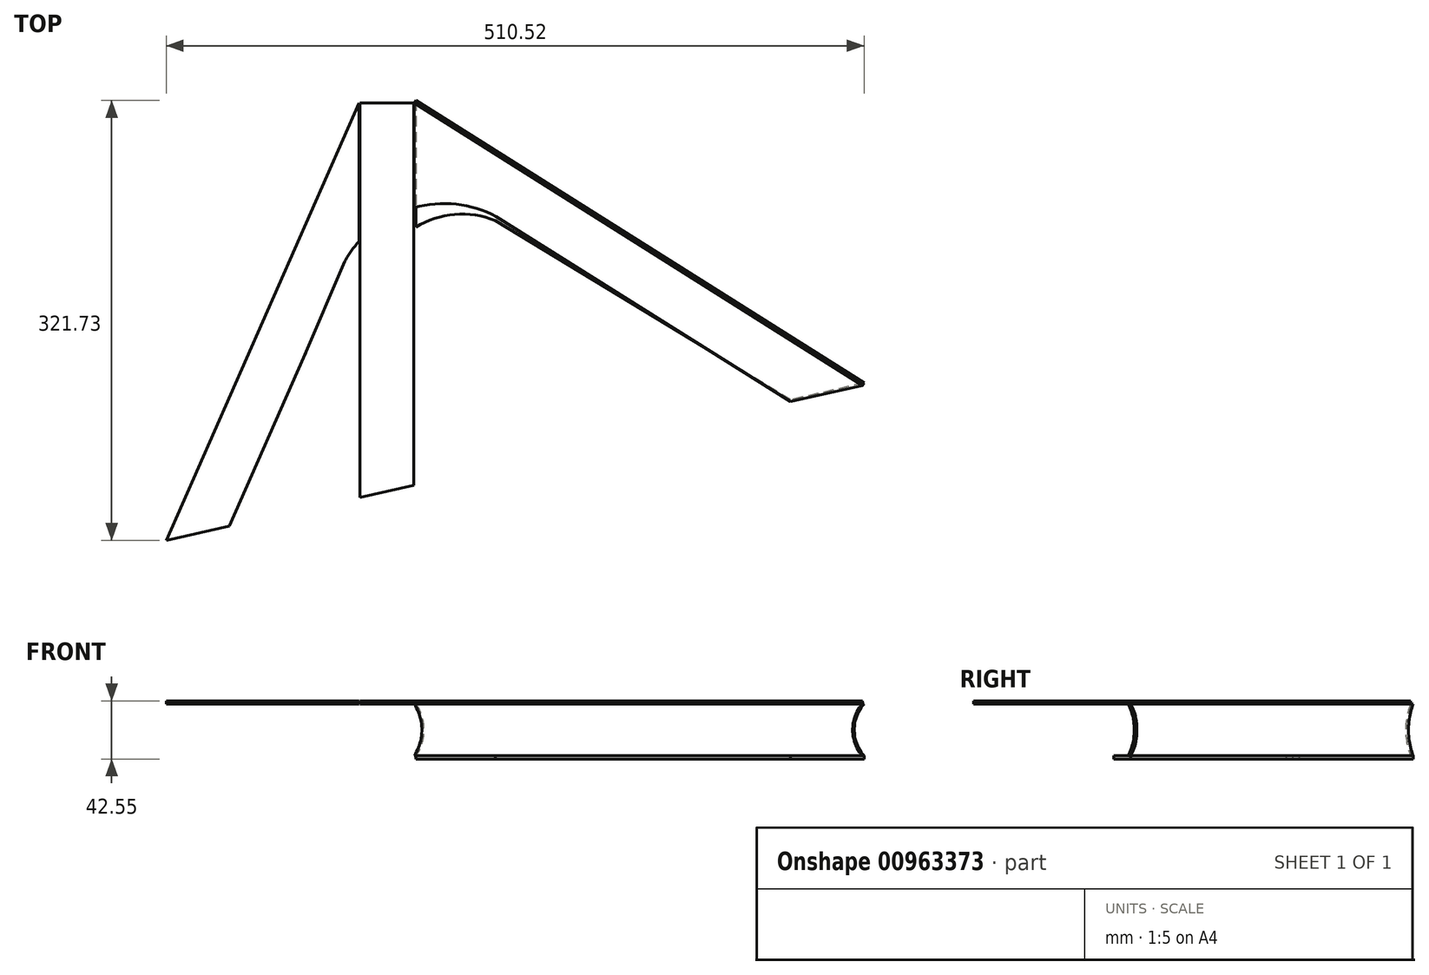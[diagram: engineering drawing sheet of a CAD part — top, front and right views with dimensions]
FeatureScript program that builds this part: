
annotation { "Feature Type Name" : "Feature", "Feature Type Description" : "" }
export const myFeature = defineFeature(function(context is Context, id is Id, definition is map)
    precondition{}
    {
        {
            var Q0;
            Q0=qCreatedBy(makeId("Top.planeOp"),FACE);
            var sketch = newSketch(context, id + "F0", { "sketchPlane" : qUnion([Q0])});
            skLineSegment(sketch, "E0", {"start": v(-23.6, 84.54) * mm, "end": v(27.72, 84.54) * mm, "construction": true});
            skLineSegment(sketch, "E1", {"start": v(27.72, 84.54) * mm, "end": v(27.72, -74.21) * mm, "construction": true});
            skLineSegment(sketch, "E2", {"start": v(27.72, -74.21) * mm, "end": v(-23.6, -74.21) * mm, "construction": true});
            skLineSegment(sketch, "E3", {"start": v(-23.6, -74.21) * mm, "end": v(-23.6, 84.54) * mm, "construction": true});
            skLineSegment(sketch, "E4", {"start": v(-152.74, -254.62) * mm, "end": v(367.67, -142.42) * mm, "construction": true});
            skLineSegment(sketch, "E5", {"start": v(367.67, -142.42) * mm, "end": v(27.72, 71.84) * mm, "construction": true});
            skLineSegment(sketch, "E6", {"start": v(-17.03, 71.84) * mm, "end": v(-158.62, -244.47) * mm, "construction": true});
            skLineSegment(sketch, "E7", {"start": v(-17.03, 71.84) * mm, "end": v(27.72, 71.84) * mm, "construction": true});
            skLineSegment(sketch, "E8", {"start": v(338.82, -22.65) * mm, "end": v(338.82, -196.3) * mm, "construction": true});
            skLineSegment(sketch, "E9", {"start": v(-227.54, -196.3) * mm, "end": v(-99.7, -276.87) * mm, "construction": true});
            skLineSegment(sketch, "E10", {"start": v(-144.73, -236.9) * mm, "end": v(347.37, -127.64) * mm, "construction": true});
            skLineSegment(sketch, "E11", {"start": v(3.64, 141.29) * mm, "end": v(3.64, -110.73) * mm, "construction": true});
            skLineSegment(sketch, "E12", {"start": v(-17.7, 61.46) * mm, "end": v(-17.7, -22.64) * mm});
            skLineSegment(sketch, "E13", {"start": v(-17.7, 61.46) * mm, "end": v(-17.7, 71.84) * mm});
            skLineSegment(sketch, "E14", {"start": v(-17.7, 71.84) * mm, "end": v(-17.03, 71.84) * mm});
            skLineSegment(sketch, "E15", {"start": v(22.7, 71.84) * mm, "end": v(22.7, 61.46) * mm});
            skLineSegment(sketch, "E16", {"start": v(22.7, 71.84) * mm, "end": v(350.68, -134.88) * mm});
            skLineSegment(sketch, "E17", {"start": v(338.82, -137.5) * mm, "end": v(297.84, -146.6) * mm});
            skLineSegment(sketch, "E18", {"start": v(350.68, -134.88) * mm, "end": v(338.82, -137.5) * mm});
            skPoint(sketch, "E19.end.orphan", {"position": v(22.7, -216.8) * mm});
            skLineSegment(sketch, "E20", {"start": v(-17.7, 71.84) * mm, "end": v(-158.62, -247.96) * mm});
            skPoint(sketch, "E21.orphan", {"position": v(0, 17.51) * mm});
            skLineSegment(sketch, "E22", {"start": v(-102.68, -215.51) * mm, "end": v(-112.47, -237.71) * mm});
            skLineSegment(sketch, "E23.trimOffspring", {"start": v(-112.47, -237.71) * mm, "end": v(-158.62, -247.96) * mm});
            skArc(sketch, "E24", {"start": v(-142.89, -244.47) * mm, "mid": v(-148.93, -241.24) * mm, "end": v(-155.78, -241.52) * mm});
            skPoint(sketch, "E25", {"position": v(22.7, -22.64) * mm});
            skArc(sketch, "E26", {"start": v(93.93, -18.1) * mm, "mid": v(90.59, -15.81) * mm, "end": v(87.1, -13.78) * mm});
            skLineSegment(sketch, "E27.trimOffspring", {"start": v(87.1, -13.78) * mm, "end": v(297.84, -146.6) * mm});
            skLineSegment(sketch, "E28.trimOffspring", {"start": v(22.7, -4.53) * mm, "end": v(22.7, 61.46) * mm});
            skLineSegment(sketch, "E29", {"start": v(22.7, -22.64) * mm, "end": v(-17.7, -61.25) * mm, "construction": true});
            skLineSegment(sketch, "E30", {"start": v(-17.7, -22.64) * mm, "end": v(-17.7, -29.37) * mm});
            skLineSegment(sketch, "E31.trimOffspring", {"start": v(-56.72, -111.21) * mm, "end": v(-102.68, -215.51) * mm});
            skLineSegment(sketch, "E32", {"start": v(-17.03, 71.84) * mm, "end": v(-17.03, -216.52) * mm});
            skLineSegment(sketch, "E33", {"start": v(22.47, 71.84) * mm, "end": v(22.47, -207.75) * mm});
            skLineSegment(sketch, "E34", {"start": v(-112.47, -237.71) * mm, "end": v(297.84, -146.6) * mm, "construction": true});
            skLineSegment(sketch, "E35", {"start": v(-17.03, -216.52) * mm, "end": v(22.47, -207.75) * mm});
            skLineSegment(sketch, "E36", {"start": v(-17.03, 71.84) * mm, "end": v(22.47, 71.84) * mm});
            skLineSegment(sketch, "E37", {"start": v(-58.12, -114.38) * mm, "end": v(-28.1, -43.83) * mm});
            skLineSegment(sketch, "E38", {"start": v(93.93, -18.1) * mm, "end": v(27.72, 23.63) * mm, "construction": true});
            skArc(sketch, "E39", {"start": v(82.85, -11.11) * mm, "mid": v(53.4, -2.17) * mm, "end": v(22.7, -4.53) * mm});
            skPoint(sketch, "E40.orphan", {"position": v(-9.44, 0) * mm});
            skArc(sketch, "E41.trimOffspring", {"start": v(-17.7, -29.37) * mm, "mid": v(-23.28, -36.32) * mm, "end": v(-28.1, -43.83) * mm});
            skLineSegment(sketch, "E42.trimOffspring", {"start": v(-23.6, -66.9) * mm, "end": v(-35.48, -78.25) * mm, "construction": true});
            skArc(sketch, "E43.trimOffspring", {"start": v(-56.72, -111.21) * mm, "mid": v(-57.43, -112.8) * mm, "end": v(-58.12, -114.38) * mm});
            skLineSegment(sketch, "E44", {"start": v(87.1, -13.78) * mm, "end": v(82.85, -11.11) * mm});
            skSolve(sketch);
        }
        {
            var Q0;
            Q0=qSketchRegion(id+"F0",true);
            extrude(context, id + "F1", {"entities" : qUnion([Q0]), "depth" : 2.3 * mm, "offsetDistance" : 25.4 * mm});
        }
        {
            var Q0;
            Q0=makeQuery(id+"F1.opExtrude","SWEPT_FACE",FACE,{"disambiguationData":[OSD([sQuery(id+"F0.wireOp",EDGE,"E16")])]});
            var sketch = newSketch(context, id + "F2", { "sketchPlane" : qUnion([Q0])});
            skLineSegment(sketch, "E45.bottom", {"start": v(19.1, 0) * mm, "end": v(-368.59, 0) * mm});
            skLineSegment(sketch, "E45.top", {"start": v(19.1, -37.97) * mm, "end": v(-368.59, -37.97) * mm});
            skArc(sketch, "E46", {"start": v(19.1, 0) * mm, "mid": v(12.47, -18.99) * mm, "end": v(19.1, -37.97) * mm});
            skArc(sketch, "E47", {"start": v(-368.59, -37.97) * mm, "mid": v(-360.1, -18.99) * mm, "end": v(-368.59, 0) * mm});
            skSolve(sketch);
        }
        {
            var Q0;
            Q0=qSketchRegion(id+"F2",true);
            extrude(context, id + "F3", {"entities" : qUnion([Q0]), "depth" : 2.3 * mm, "offsetDistance" : 25.4 * mm});
        }
        {
            var Q0;
            Q0=makeQuery(id+"F3.opExtrude","SWEPT_FACE",FACE,{"disambiguationData":[OSD([sQuery(id+"F2.wireOp",EDGE,"E45.top")])]});
            var sketch = newSketch(context, id + "F4", { "sketchPlane" : qUnion([Q0])});
            skLineSegment(sketch, "E48", {"start": v(23.91, -73.77) * mm, "end": v(351.9, 132.94) * mm});
            skLineSegment(sketch, "E49", {"start": v(297.9, 145.23) * mm, "end": v(82.04, 14.06) * mm});
            skLineSegment(sketch, "E50", {"start": v(351.9, 132.94) * mm, "end": v(297.9, 145.23) * mm});
            skArc(sketch, "E51", {"start": v(23.91, 18.93) * mm, "mid": v(52.4, 9.65) * mm, "end": v(82.04, 14.06) * mm});
            skPoint(sketch, "E52.start.orphan", {"position": v(23.91, -21.26) * mm});
            skLineSegment(sketch, "E53", {"start": v(23.91, -73.77) * mm, "end": v(23.91, 18.93) * mm});
            skSolve(sketch);
        }
        {
            var Q0;
            Q0=qSketchRegion(id+"F4",true);
            extrude(context, id + "F5", {"entities" : qUnion([Q0]), "depth" : 2.3 * mm, "offsetDistance" : 25.4 * mm});
        }
    });
